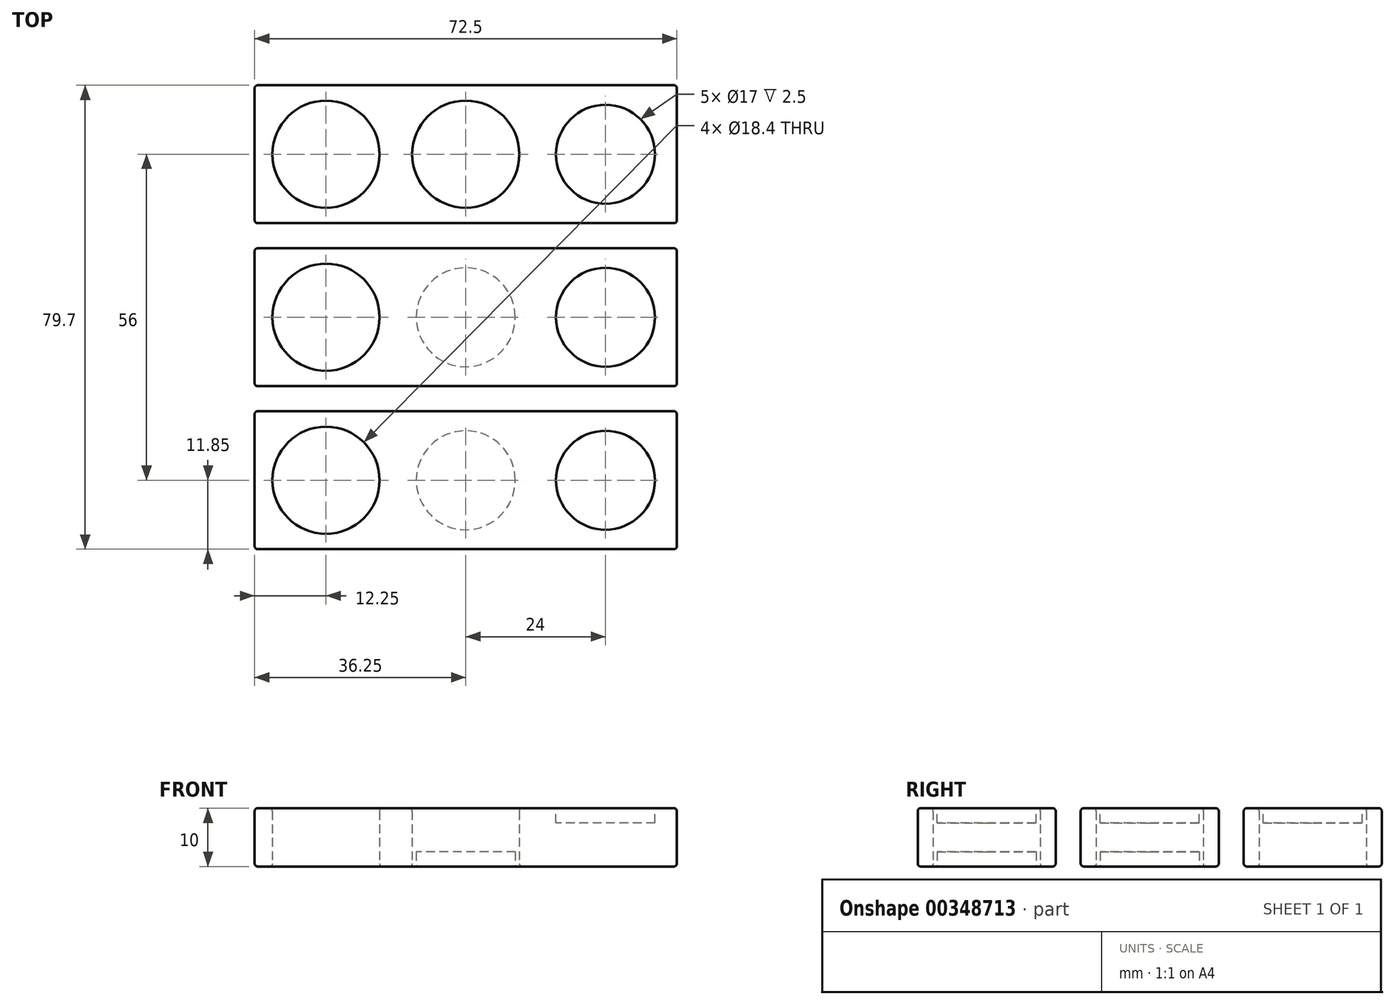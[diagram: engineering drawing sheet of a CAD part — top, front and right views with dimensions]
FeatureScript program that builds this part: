
annotation { "Feature Type Name" : "Feature", "Feature Type Description" : "" }
export const myFeature = defineFeature(function(context is Context, id is Id, definition is map)
    precondition{}
    {
        {
            var Q0;
            Q0=qCreatedBy(makeId("Top.planeOp"),FACE);
            var sketch = newSketch(context, id + "F0", { "sketchPlane" : qUnion([Q0])});
            skLineSegment(sketch, "E0", {"start": v(0, 0) * mm, "end": v(0, -99.1) * mm, "construction": true});
            skLineSegment(sketch, "E1.bottom", {"start": v(0, 0) * mm, "end": v(72.5, 0) * mm});
            skLineSegment(sketch, "E1.top", {"start": v(0, -23.7) * mm, "end": v(72.5, -23.7) * mm});
            skLineSegment(sketch, "E1.left", {"start": v(0, 0) * mm, "end": v(0, -23.7) * mm});
            skLineSegment(sketch, "E1.right", {"start": v(72.5, 0) * mm, "end": v(72.5, -23.7) * mm});
            skLineSegment(sketch, "E2.0.1.0", {"start": v(72.5, -28) * mm, "end": v(72.5, -51.7) * mm});
            skLineSegment(sketch, "E2.0.1.1", {"start": v(0, -51.7) * mm, "end": v(72.5, -51.7) * mm});
            skLineSegment(sketch, "E2.0.1.2", {"start": v(0, -28) * mm, "end": v(72.5, -28) * mm});
            skLineSegment(sketch, "E2.0.1.3", {"start": v(0, -28) * mm, "end": v(0, -51.7) * mm});
            skLineSegment(sketch, "E2.0.2.0", {"start": v(72.5, -56) * mm, "end": v(72.5, -79.7) * mm});
            skLineSegment(sketch, "E2.0.2.1", {"start": v(0, -79.7) * mm, "end": v(72.5, -79.7) * mm});
            skLineSegment(sketch, "E2.0.2.2", {"start": v(0, -56) * mm, "end": v(72.5, -56) * mm});
            skLineSegment(sketch, "E2.0.2.3", {"start": v(0, -56) * mm, "end": v(0, -79.7) * mm});
            skLineSegment(sketch, "E2.0.3.0", {"start": v(72.5, -84) * mm, "end": v(72.5, -107.7) * mm});
            skLineSegment(sketch, "E2.0.3.1", {"start": v(0, -107.7) * mm, "end": v(72.5, -107.7) * mm});
            skLineSegment(sketch, "E2.0.3.2", {"start": v(0, -84) * mm, "end": v(72.5, -84) * mm});
            skLineSegment(sketch, "E2.0.3.3", {"start": v(0, -84) * mm, "end": v(0, -107.7) * mm});
            skLineSegment(sketch, "E2.0.4.0", {"start": v(72.5, -112) * mm, "end": v(72.5, -135.7) * mm});
            skLineSegment(sketch, "E2.0.4.1", {"start": v(0, -135.7) * mm, "end": v(72.5, -135.7) * mm});
            skLineSegment(sketch, "E2.0.4.2", {"start": v(0, -112) * mm, "end": v(72.5, -112) * mm});
            skLineSegment(sketch, "E2.0.4.3", {"start": v(0, -112) * mm, "end": v(0, -135.7) * mm});
            skLineSegment(sketch, "E2.0.5.0", {"start": v(72.5, -140) * mm, "end": v(72.5, -163.7) * mm});
            skLineSegment(sketch, "E2.0.5.1", {"start": v(0, -163.7) * mm, "end": v(72.5, -163.7) * mm});
            skLineSegment(sketch, "E2.0.5.2", {"start": v(0, -140) * mm, "end": v(72.5, -140) * mm});
            skLineSegment(sketch, "E2.0.5.3", {"start": v(0, -140) * mm, "end": v(0, -163.7) * mm});
            skLineSegment(sketch, "E2.direction1", {"start": v(72.5, -23.7) * mm, "end": v(97.83, -23.7) * mm, "construction": true});
            skLineSegment(sketch, "E2.direction2", {"start": v(72.5, -23.7) * mm, "end": v(72.5, -51.7) * mm, "construction": true});
            skLineSegment(sketch, "E3", {"start": v(0, -11.85) * mm, "end": v(12.25, -11.85) * mm, "construction": true});
            skLineSegment(sketch, "E4", {"start": v(12.25, -11.85) * mm, "end": v(36.25, -11.85) * mm, "construction": true});
            skLineSegment(sketch, "E5", {"start": v(36.25, -11.85) * mm, "end": v(60.25, -11.85) * mm, "construction": true});
            skLineSegment(sketch, "E6", {"start": v(60.25, -11.85) * mm, "end": v(72.5, -11.85) * mm, "construction": true});
            skLineSegment(sketch, "E7", {"start": v(12.25, -11.85) * mm, "end": v(12.25, -182.05) * mm, "construction": true});
            skLineSegment(sketch, "E8", {"start": v(36.25, -11.85) * mm, "end": v(36.25, -186.32) * mm, "construction": true});
            skLineSegment(sketch, "E9", {"start": v(60.25, -11.85) * mm, "end": v(60.25, -189.7) * mm, "construction": true});
            skCircle(sketch, "E10", {"center": v(12.25, -11.85) * mm, "radius": 9.2 * mm});
            skCircle(sketch, "E11", {"center": v(36.25, -11.85) * mm, "radius": 9.2 * mm});
            skLineSegment(sketch, "E12", {"start": v(0, -39.85) * mm, "end": v(72.5, -39.85) * mm, "construction": true});
            skLineSegment(sketch, "E13", {"start": v(0, -67.85) * mm, "end": v(72.5, -67.85) * mm, "construction": true});
            skLineSegment(sketch, "E14", {"start": v(0, -95.85) * mm, "end": v(72.5, -95.85) * mm, "construction": true});
            skLineSegment(sketch, "E15", {"start": v(0, -123.85) * mm, "end": v(72.5, -123.85) * mm, "construction": true});
            skLineSegment(sketch, "E16", {"start": v(0, -151.85) * mm, "end": v(72.5, -151.85) * mm, "construction": true});
            skCircle(sketch, "E17", {"center": v(12.25, -39.85) * mm, "radius": 9.2 * mm});
            skCircle(sketch, "E18", {"center": v(12.25, -67.85) * mm, "radius": 9.2 * mm});
            skCircle(sketch, "E19", {"center": v(36.25, -95.85) * mm, "radius": 9.2 * mm});
            skCircle(sketch, "E20", {"center": v(36.25, -39.85) * mm, "radius": 8.5 * mm});
            skCircle(sketch, "E21", {"center": v(36.25, -67.85) * mm, "radius": 8.5 * mm});
            skCircle(sketch, "E22", {"center": v(12.25, -95.85) * mm, "radius": 8.5 * mm});
            skCircle(sketch, "E23", {"center": v(36.25, -123.85) * mm, "radius": 8.5 * mm});
            skCircle(sketch, "E24", {"center": v(12.25, -151.85) * mm, "radius": 8.5 * mm});
            skSolve(sketch);
        }
        {
            var Q0;
            Q0=makeQuery(id+"F0.imprint","IMPRINT",FACE,{"disambiguationData":[TD([[makeQuery(id+"F0.imprint","IMPRINT",EDGE,{"derivedFrom":sQuery(id+"F0.wireOp",EDGE,"E1.bottom")}),-1.0]])]});
            var Q1;
            Q1=makeQuery(id+"F0.imprint","IMPRINT",FACE,{"disambiguationData":[TD([[makeQuery(id+"F0.imprint","IMPRINT",EDGE,{"derivedFrom":sQuery(id+"F0.wireOp",EDGE,"E2.0.1.0")}),-1.0]])]});
            var Q2;
            Q2=makeQuery(id+"F0.imprint","IMPRINT",FACE,{"disambiguationData":[TD([[makeQuery(id+"F0.imprint","IMPRINT",EDGE,{"derivedFrom":sQuery(id+"F0.wireOp",EDGE,"E2.0.2.0")}),-1.0]])]});
            var Q3;
            Q3=makeQuery(id+"F0.imprint","IMPRINT",FACE,{"disambiguationData":[TD([[makeQuery(id+"F0.imprint","IMPRINT",EDGE,{"derivedFrom":sQuery(id+"F0.wireOp",EDGE,"E2.0.3.0")}),-1.0]])]});
            var Q4;
            Q4=makeQuery(id+"F0.imprint","IMPRINT",FACE,{"disambiguationData":[TD([[makeQuery(id+"F0.imprint","IMPRINT",EDGE,{"derivedFrom":sQuery(id+"F0.wireOp",EDGE,"E2.0.4.0")}),-1.0]])]});
            var Q5;
            Q5=makeQuery(id+"F0.imprint","IMPRINT",FACE,{"disambiguationData":[TD([[makeQuery(id+"F0.imprint","IMPRINT",EDGE,{"derivedFrom":sQuery(id+"F0.wireOp",EDGE,"E2.0.5.0")}),-1.0]])]});
            var Q6;
            Q6=makeQuery(id+"F0.imprint","IMPRINT",FACE,{"disambiguationData":[TD([[makeQuery(id+"F0.imprint","IMPRINT",EDGE,{"derivedFrom":sQuery(id+"F0.wireOp",EDGE,"E23")}),1.0]])]});
            var Q7;
            Q7=makeQuery(id+"F0.imprint","IMPRINT",FACE,{"disambiguationData":[TD([[makeQuery(id+"F0.imprint","IMPRINT",EDGE,{"derivedFrom":sQuery(id+"F0.wireOp",EDGE,"E24")}),1.0]])]});
            var Q8;
            Q8=makeQuery(id+"F0.imprint","IMPRINT",FACE,{"disambiguationData":[TD([[makeQuery(id+"F0.imprint","IMPRINT",EDGE,{"derivedFrom":sQuery(id+"F0.wireOp",EDGE,"E21")}),1.0]])]});
            var Q9;
            Q9=makeQuery(id+"F0.imprint","IMPRINT",FACE,{"disambiguationData":[TD([[makeQuery(id+"F0.imprint","IMPRINT",EDGE,{"derivedFrom":sQuery(id+"F0.wireOp",EDGE,"E20")}),1.0]])]});
            var Q10;
            Q10=makeQuery(id+"F0.imprint","IMPRINT",FACE,{"disambiguationData":[TD([[makeQuery(id+"F0.imprint","IMPRINT",EDGE,{"derivedFrom":sQuery(id+"F0.wireOp",EDGE,"E22")}),1.0]])]});
            extrude(context, id + "F1", {"entities" : qUnion([Q0, Q1, Q2, Q3, Q4, Q5, Q6, Q7, Q8, Q9, Q10]), "depth" : 10 * mm});
        }
        {
            var Q0;
            Q0=makeQuery(id+"F0.imprint","IMPRINT",FACE,{"disambiguationData":[TD([[makeQuery(id+"F0.imprint","IMPRINT",EDGE,{"derivedFrom":sQuery(id+"F0.wireOp",EDGE,"E24")}),1.0]])]});
            var Q1;
            Q1=makeQuery(id+"F0.imprint","IMPRINT",FACE,{"disambiguationData":[TD([[makeQuery(id+"F0.imprint","IMPRINT",EDGE,{"derivedFrom":sQuery(id+"F0.wireOp",EDGE,"E23")}),1.0]])]});
            var Q2;
            Q2=makeQuery(id+"F0.imprint","IMPRINT",FACE,{"disambiguationData":[TD([[makeQuery(id+"F0.imprint","IMPRINT",EDGE,{"derivedFrom":sQuery(id+"F0.wireOp",EDGE,"E22")}),1.0]])]});
            var Q3;
            Q3=makeQuery(id+"F0.imprint","IMPRINT",FACE,{"disambiguationData":[TD([[makeQuery(id+"F0.imprint","IMPRINT",EDGE,{"derivedFrom":sQuery(id+"F0.wireOp",EDGE,"E21")}),1.0]])]});
            var Q4;
            Q4=makeQuery(id+"F0.imprint","IMPRINT",FACE,{"disambiguationData":[TD([[makeQuery(id+"F0.imprint","IMPRINT",EDGE,{"derivedFrom":sQuery(id+"F0.wireOp",EDGE,"E20")}),1.0]])]});
            extrude(context, id + "F2", {"entities" : qUnion([Q0, Q1, Q2, Q3, Q4]), "operationType" : NewBodyOperationType.REMOVE, "depth" : 2.5 * mm});
        }
        {
            var Q0;
            Q0=makeQuery(id+"F1.opExtrude","CAP_FACE",FACE,{"disambiguationData":[OSD([sQuery(id+"F0.wireOp",EDGE,"E2.0.5.0"),sQuery(id+"F0.wireOp",EDGE,"E2.0.5.1"),sQuery(id+"F0.wireOp",EDGE,"E2.0.5.2"),sQuery(id+"F0.wireOp",EDGE,"E2.0.5.3")])],"isStart":false});
            var sketch = newSketch(context, id + "F3", { "sketchPlane" : qUnion([Q0])});
            skCircle(sketch, "E25", {"center": v(60.25, -11.85) * mm, "radius": 8.5 * mm});
            skCircle(sketch, "E26", {"center": v(60.25, -39.85) * mm, "radius": 8.5 * mm});
            skCircle(sketch, "E27", {"center": v(60.25, -67.85) * mm, "radius": 8.5 * mm});
            skCircle(sketch, "E28", {"center": v(60.25, -95.85) * mm, "radius": 8.5 * mm});
            skCircle(sketch, "E29", {"center": v(60.25, -123.85) * mm, "radius": 8.5 * mm});
            skCircle(sketch, "E30", {"center": v(12.25, -123.85) * mm, "radius": 8.5 * mm});
            skCircle(sketch, "E31", {"center": v(36.25, -151.85) * mm, "radius": 8.5 * mm});
            skCircle(sketch, "E32", {"center": v(60.25, -151.85) * mm, "radius": 8.5 * mm});
            skLineSegment(sketch, "E33", {"start": v(36.25, -163.7) * mm, "end": v(36.25, 0) * mm, "construction": true});
            skPoint(sketch, "E34.startSnap0", {"position": v(0, -151.85) * mm});
            skLineSegment(sketch, "E35", {"start": v(0, -151.85) * mm, "end": v(0, -125.8) * mm, "construction": true});
            skLineSegment(sketch, "E36", {"start": v(0, -151.85) * mm, "end": v(12.25, -151.85) * mm, "construction": true});
            skLineSegment(sketch, "E37", {"start": v(12.25, -151.85) * mm, "end": v(36.25, -151.85) * mm, "construction": true});
            skLineSegment(sketch, "E38", {"start": v(36.25, -151.85) * mm, "end": v(60.25, -151.85) * mm, "construction": true});
            skLineSegment(sketch, "E39", {"start": v(60.25, -151.85) * mm, "end": v(72.5, -151.85) * mm, "construction": true});
            skLineSegment(sketch, "E40.0.1.0", {"start": v(0, -123.85) * mm, "end": v(12.25, -123.85) * mm, "construction": true});
            skLineSegment(sketch, "E40.0.1.1", {"start": v(12.25, -123.85) * mm, "end": v(36.25, -123.85) * mm, "construction": true});
            skLineSegment(sketch, "E40.0.1.2", {"start": v(36.25, -123.85) * mm, "end": v(60.25, -123.85) * mm, "construction": true});
            skLineSegment(sketch, "E40.0.1.3", {"start": v(60.25, -123.85) * mm, "end": v(72.5, -123.85) * mm, "construction": true});
            skLineSegment(sketch, "E40.0.2.0", {"start": v(0, -95.85) * mm, "end": v(12.25, -95.85) * mm, "construction": true});
            skLineSegment(sketch, "E40.0.2.1", {"start": v(12.25, -95.85) * mm, "end": v(36.25, -95.85) * mm, "construction": true});
            skLineSegment(sketch, "E40.0.2.2", {"start": v(36.25, -95.85) * mm, "end": v(60.25, -95.85) * mm, "construction": true});
            skLineSegment(sketch, "E40.0.2.3", {"start": v(60.25, -95.85) * mm, "end": v(72.5, -95.85) * mm, "construction": true});
            skLineSegment(sketch, "E40.0.3.0", {"start": v(0, -67.85) * mm, "end": v(12.25, -67.85) * mm, "construction": true});
            skLineSegment(sketch, "E40.0.3.1", {"start": v(12.25, -67.85) * mm, "end": v(36.25, -67.85) * mm, "construction": true});
            skLineSegment(sketch, "E40.0.3.2", {"start": v(36.25, -67.85) * mm, "end": v(60.25, -67.85) * mm, "construction": true});
            skLineSegment(sketch, "E40.0.3.3", {"start": v(60.25, -67.85) * mm, "end": v(72.5, -67.85) * mm, "construction": true});
            skLineSegment(sketch, "E40.0.4.0", {"start": v(0, -39.85) * mm, "end": v(12.25, -39.85) * mm, "construction": true});
            skLineSegment(sketch, "E40.0.4.1", {"start": v(12.25, -39.85) * mm, "end": v(36.25, -39.85) * mm, "construction": true});
            skLineSegment(sketch, "E40.0.4.2", {"start": v(36.25, -39.85) * mm, "end": v(60.25, -39.85) * mm, "construction": true});
            skLineSegment(sketch, "E40.0.4.3", {"start": v(60.25, -39.85) * mm, "end": v(72.5, -39.85) * mm, "construction": true});
            skLineSegment(sketch, "E40.0.5.0", {"start": v(0, -11.85) * mm, "end": v(12.25, -11.85) * mm, "construction": true});
            skLineSegment(sketch, "E40.0.5.1", {"start": v(12.25, -11.85) * mm, "end": v(36.25, -11.85) * mm, "construction": true});
            skLineSegment(sketch, "E40.0.5.2", {"start": v(36.25, -11.85) * mm, "end": v(60.25, -11.85) * mm, "construction": true});
            skLineSegment(sketch, "E40.0.5.3", {"start": v(60.25, -11.85) * mm, "end": v(72.5, -11.85) * mm, "construction": true});
            skLineSegment(sketch, "E40.direction1", {"start": v(0, -151.85) * mm, "end": v(25, -151.85) * mm, "construction": true});
            skLineSegment(sketch, "E40.direction2", {"start": v(0, -151.85) * mm, "end": v(0, -123.85) * mm, "construction": true});
            skSolve(sketch);
        }
        {
            var Q0;
            Q0=makeQuery(id+"F3.imprint","IMPRINT",FACE,{"disambiguationData":[TD([[makeQuery(id+"F3.imprint","IMPRINT",EDGE,{"derivedFrom":sQuery(id+"F3.wireOp",EDGE,"E30")}),1.0]])]});
            var Q1;
            Q1=makeQuery(id+"F3.imprint","IMPRINT",FACE,{"disambiguationData":[TD([[makeQuery(id+"F3.imprint","IMPRINT",EDGE,{"derivedFrom":sQuery(id+"F3.wireOp",EDGE,"E31")}),1.0]])]});
            var Q2;
            Q2=makeQuery(id+"F3.imprint","IMPRINT",FACE,{"disambiguationData":[TD([[makeQuery(id+"F3.imprint","IMPRINT",EDGE,{"derivedFrom":sQuery(id+"F3.wireOp",EDGE,"E32")}),1.0]])]});
            var Q3;
            Q3=makeQuery(id+"F3.imprint","IMPRINT",FACE,{"disambiguationData":[TD([[makeQuery(id+"F3.imprint","IMPRINT",EDGE,{"derivedFrom":sQuery(id+"F3.wireOp",EDGE,"E29")}),1.0]])]});
            var Q4;
            Q4=makeQuery(id+"F3.imprint","IMPRINT",FACE,{"disambiguationData":[TD([[makeQuery(id+"F3.imprint","IMPRINT",EDGE,{"derivedFrom":sQuery(id+"F3.wireOp",EDGE,"E28")}),1.0]])]});
            var Q5;
            Q5=makeQuery(id+"F3.imprint","IMPRINT",FACE,{"disambiguationData":[TD([[makeQuery(id+"F3.imprint","IMPRINT",EDGE,{"derivedFrom":sQuery(id+"F3.wireOp",EDGE,"E27")}),1.0]])]});
            var Q6;
            Q6=makeQuery(id+"F3.imprint","IMPRINT",FACE,{"disambiguationData":[TD([[makeQuery(id+"F3.imprint","IMPRINT",EDGE,{"derivedFrom":sQuery(id+"F3.wireOp",EDGE,"E26")}),1.0]])]});
            var Q7;
            Q7=makeQuery(id+"F3.imprint","IMPRINT",FACE,{"disambiguationData":[TD([[makeQuery(id+"F3.imprint","IMPRINT",EDGE,{"derivedFrom":sQuery(id+"F3.wireOp",EDGE,"E25")}),1.0]])]});
            extrude(context, id + "F4", {"entities" : qUnion([Q0, Q1, Q2, Q3, Q4, Q5, Q6, Q7]), "operationType" : NewBodyOperationType.REMOVE, "oppositeDirection" : true, "depth" : 2.5 * mm});
        }
        {
            var Q0;
            Q0=makeQuery(id+"F1.opExtrude","SWEPT_FACE",FACE,{"disambiguationData":[OSD([sQuery(id+"F0.wireOp",EDGE,"E2.0.5.1")])]});
            var Q1;
            Q1=makeQuery(id+"F1.opExtrude","SWEPT_FACE",FACE,{"disambiguationData":[OSD([sQuery(id+"F0.wireOp",EDGE,"E2.0.5.0")])]});
            var Q2;
            Q2=makeQuery(id+"F1.opExtrude","SWEPT_FACE",FACE,{"disambiguationData":[OSD([sQuery(id+"F0.wireOp",EDGE,"E2.0.4.0")])]});
            var Q3;
            Q3=makeQuery(id+"F1.opExtrude","SWEPT_FACE",FACE,{"disambiguationData":[OSD([sQuery(id+"F0.wireOp",EDGE,"E2.0.3.0")])]});
            var Q4;
            Q4=makeQuery(id+"F1.opExtrude","SWEPT_FACE",FACE,{"disambiguationData":[OSD([sQuery(id+"F0.wireOp",EDGE,"E2.0.2.0")])]});
            var Q5;
            Q5=makeQuery(id+"F1.opExtrude","SWEPT_FACE",FACE,{"disambiguationData":[OSD([sQuery(id+"F0.wireOp",EDGE,"E2.0.1.0")])]});
            var Q6;
            Q6=makeQuery(id+"F1.opExtrude","SWEPT_FACE",FACE,{"disambiguationData":[OSD([sQuery(id+"F0.wireOp",EDGE,"E1.right")])]});
            var Q7;
            Q7=makeQuery(id+"F1.opExtrude","SWEPT_FACE",FACE,{"disambiguationData":[OSD([sQuery(id+"F0.wireOp",EDGE,"E1.bottom")])]});
            var Q8;
            Q8=makeQuery(id+"F1.opExtrude","SWEPT_FACE",FACE,{"disambiguationData":[OSD([sQuery(id+"F0.wireOp",EDGE,"E1.left")])]});
            var Q9;
            Q9=makeQuery(id+"F1.opExtrude","SWEPT_FACE",FACE,{"disambiguationData":[OSD([sQuery(id+"F0.wireOp",EDGE,"E2.0.1.3")])]});
            var Q10;
            Q10=makeQuery(id+"F1.opExtrude","SWEPT_FACE",FACE,{"disambiguationData":[OSD([sQuery(id+"F0.wireOp",EDGE,"E2.0.2.3")])]});
            var Q11;
            Q11=makeQuery(id+"F1.opExtrude","SWEPT_FACE",FACE,{"disambiguationData":[OSD([sQuery(id+"F0.wireOp",EDGE,"E2.0.3.3")])]});
            var Q12;
            Q12=makeQuery(id+"F1.opExtrude","SWEPT_FACE",FACE,{"disambiguationData":[OSD([sQuery(id+"F0.wireOp",EDGE,"E2.0.4.3")])]});
            var Q13;
            Q13=makeQuery(id+"F1.opExtrude","SWEPT_FACE",FACE,{"disambiguationData":[OSD([sQuery(id+"F0.wireOp",EDGE,"E2.0.5.3")])]});
            var Q14;
            Q14=makeQuery(id+"F1.opExtrude","SWEPT_FACE",FACE,{"disambiguationData":[OSD([sQuery(id+"F0.wireOp",EDGE,"E2.0.5.2")])]});
            var Q15;
            Q15=makeQuery(id+"F1.opExtrude","SWEPT_FACE",FACE,{"disambiguationData":[OSD([sQuery(id+"F0.wireOp",EDGE,"E2.0.4.2")])]});
            var Q16;
            Q16=makeQuery(id+"F1.opExtrude","SWEPT_FACE",FACE,{"disambiguationData":[OSD([sQuery(id+"F0.wireOp",EDGE,"E2.0.3.2")])]});
            var Q17;
            Q17=makeQuery(id+"F1.opExtrude","SWEPT_FACE",FACE,{"disambiguationData":[OSD([sQuery(id+"F0.wireOp",EDGE,"E2.0.2.2")])]});
            var Q18;
            Q18=makeQuery(id+"F1.opExtrude","SWEPT_FACE",FACE,{"disambiguationData":[OSD([sQuery(id+"F0.wireOp",EDGE,"E2.0.1.2")])]});
            var Q19;
            Q19=makeQuery(id+"F1.opExtrude","SWEPT_FACE",FACE,{"disambiguationData":[OSD([sQuery(id+"F0.wireOp",EDGE,"E1.top")])]});
            var Q20;
            Q20=makeQuery(id+"F1.opExtrude","SWEPT_FACE",FACE,{"disambiguationData":[OSD([sQuery(id+"F0.wireOp",EDGE,"E2.0.1.1")])]});
            var Q21;
            Q21=makeQuery(id+"F1.opExtrude","SWEPT_FACE",FACE,{"disambiguationData":[OSD([sQuery(id+"F0.wireOp",EDGE,"E2.0.2.1")])]});
            var Q22;
            Q22=makeQuery(id+"F1.opExtrude","SWEPT_FACE",FACE,{"disambiguationData":[OSD([sQuery(id+"F0.wireOp",EDGE,"E2.0.3.1")])]});
            var Q23;
            Q23=makeQuery(id+"F1.opExtrude","SWEPT_FACE",FACE,{"disambiguationData":[OSD([sQuery(id+"F0.wireOp",EDGE,"E2.0.4.1")])]});
            fillet(context, id + "F5", {"entities" : qUnion([Q0, Q1, Q2, Q3, Q4, Q5, Q6, Q7, Q8, Q9, Q10, Q11, Q12, Q13, Q14, Q15, Q16, Q17, Q18, Q19, Q20, Q21, Q22, Q23]), "radius" : 0.5 * mm, "tangentPropagation" : true, "allowEdgeOverflow" : false});
        }
        {
            var Q0;
            Q0=makeQuery(id+"F1.opExtrude","SWEPT_FACE",FACE,{"disambiguationData":[OSD([sQuery(id+"F0.wireOp",EDGE,"E17")])]});
            var Q1;
            Q1=makeQuery(id+"F1.opExtrude","SWEPT_FACE",FACE,{"disambiguationData":[OSD([sQuery(id+"F0.wireOp",EDGE,"E10")])]});
            var Q2;
            Q2=makeQuery(id+"F1.opExtrude","SWEPT_FACE",FACE,{"disambiguationData":[OSD([sQuery(id+"F0.wireOp",EDGE,"E11")])]});
            var Q3;
            Q3=makeQuery(id+"F1.opExtrude","SWEPT_FACE",FACE,{"disambiguationData":[OSD([sQuery(id+"F0.wireOp",EDGE,"E18")])]});
            var Q4;
            Q4=makeQuery(id+"F1.opExtrude","SWEPT_FACE",FACE,{"disambiguationData":[OSD([sQuery(id+"F0.wireOp",EDGE,"E19")])]});
            fillet(context, id + "F6", {"entities" : qUnion([Q0, Q1, Q2, Q3, Q4]), "radius" : 0.5 * mm, "tangentPropagation" : true, "allowEdgeOverflow" : false});
        }
        {
            var Q0;
            Q0=makeQuery(id+"F1.opExtrude","SWEPT_BODY",BODY,{"disambiguationData":[OSD([sQuery(id+"F0.wireOp",EDGE,"E2.0.3.0"),sQuery(id+"F0.wireOp",EDGE,"E2.0.3.1"),sQuery(id+"F0.wireOp",EDGE,"E2.0.3.2"),sQuery(id+"F0.wireOp",EDGE,"E2.0.3.3"),sQuery(id+"F0.wireOp",EDGE,"E19")])]});
            var Q1;
            Q1=makeQuery(id+"F1.opExtrude","SWEPT_BODY",BODY,{"disambiguationData":[OSD([sQuery(id+"F0.wireOp",EDGE,"E2.0.4.0"),sQuery(id+"F0.wireOp",EDGE,"E2.0.4.1"),sQuery(id+"F0.wireOp",EDGE,"E2.0.4.2"),sQuery(id+"F0.wireOp",EDGE,"E2.0.4.3")])]});
            var Q2;
            Q2=makeQuery(id+"F1.opExtrude","SWEPT_BODY",BODY,{"disambiguationData":[OSD([sQuery(id+"F0.wireOp",EDGE,"E2.0.5.0"),sQuery(id+"F0.wireOp",EDGE,"E2.0.5.1"),sQuery(id+"F0.wireOp",EDGE,"E2.0.5.2"),sQuery(id+"F0.wireOp",EDGE,"E2.0.5.3")])]});
            deleteBodies(context, id + "F7", {"entities" : qUnion([Q0, Q1, Q2])});
        }
    });
